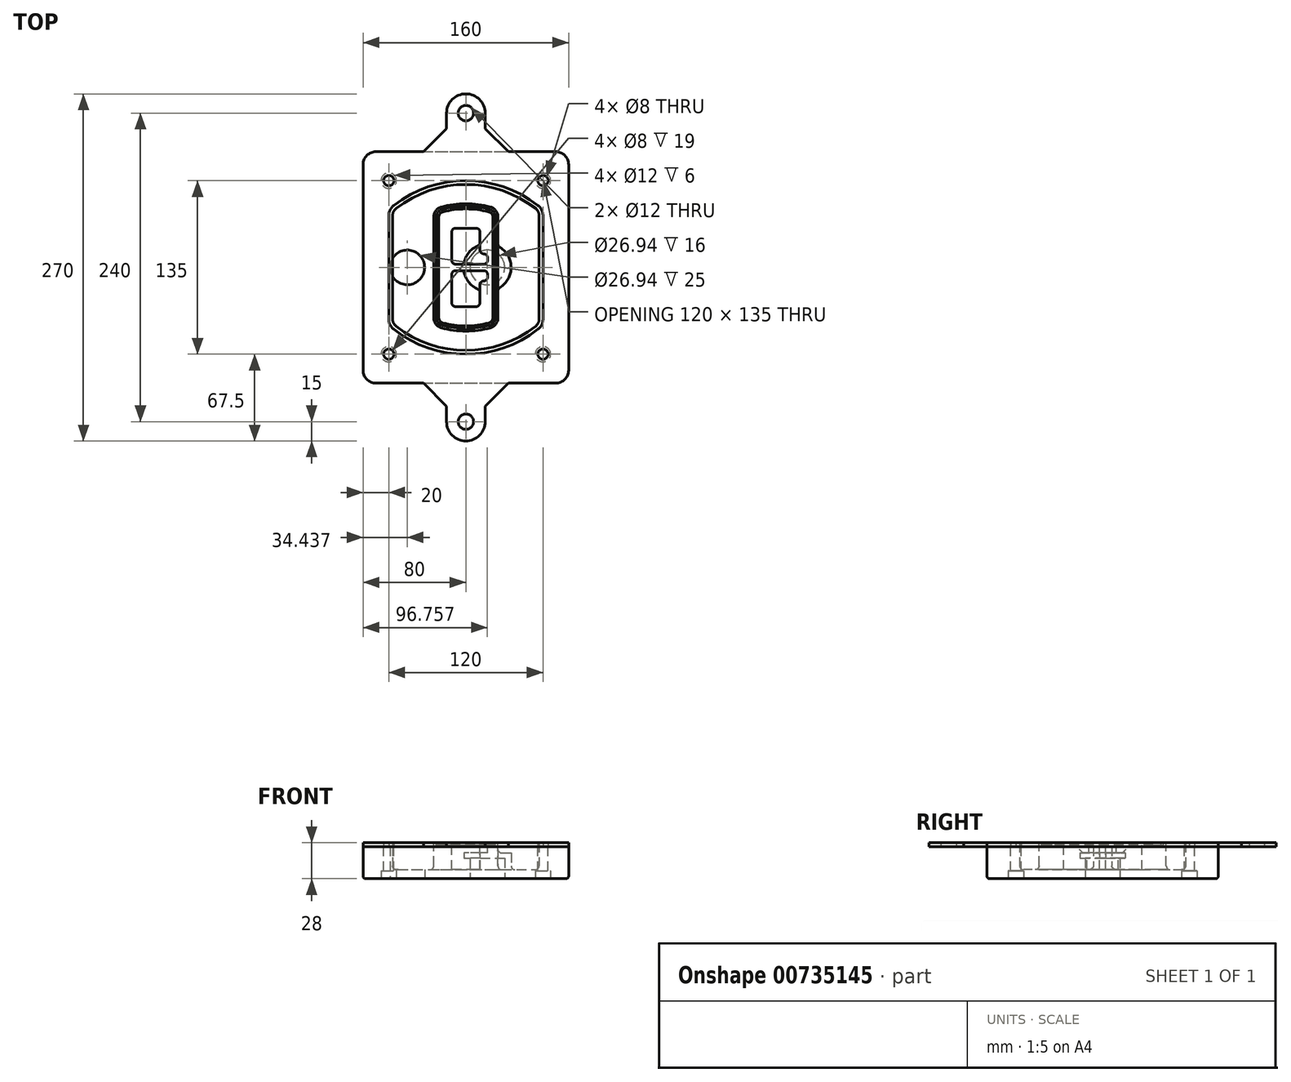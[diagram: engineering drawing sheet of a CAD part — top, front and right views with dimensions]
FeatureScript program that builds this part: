
annotation { "Feature Type Name" : "Feature", "Feature Type Description" : "" }
export const myFeature = defineFeature(function(context is Context, id is Id, definition is map)
    precondition{}
    {
        {
            var Q0;
            Q0=qCreatedBy(makeId("Top.planeOp"),FACE);
            var sketch = newSketch(context, id + "F0", { "sketchPlane" : qUnion([Q0])});
            skPoint(sketch, "E0.rect.middle", {"position": v(0, 0) * mm});
            skLineSegment(sketch, "E1.bottom", {"start": v(-70, -90) * mm, "end": v(70, -90) * mm});
            skLineSegment(sketch, "E1.top", {"start": v(-70, 90) * mm, "end": v(70, 90) * mm});
            skLineSegment(sketch, "E1.left", {"start": v(-80, -80) * mm, "end": v(-80, 80) * mm});
            skLineSegment(sketch, "E1.right", {"start": v(80, -80) * mm, "end": v(80, 80) * mm});
            skLineSegment(sketch, "E2", {"start": v(-80, 90) * mm, "end": v(80, -90) * mm, "construction": true});
            skLineSegment(sketch, "E3", {"start": v(80, 90) * mm, "end": v(-80, -90) * mm, "construction": true});
            skCircle(sketch, "E4", {"center": v(-60, 67.5) * mm, "radius": 4 * mm});
            skCircle(sketch, "E5", {"center": v(60, 67.5) * mm, "radius": 4 * mm});
            skCircle(sketch, "E6", {"center": v(60, -67.5) * mm, "radius": 4 * mm});
            skCircle(sketch, "E7", {"center": v(-60, -67.5) * mm, "radius": 4 * mm});
            skLineSegment(sketch, "E8", {"start": v(-60, 67.5) * mm, "end": v(60, 67.5) * mm, "construction": true});
            skLineSegment(sketch, "E9", {"start": v(60, 67.5) * mm, "end": v(60, -67.5) * mm, "construction": true});
            skLineSegment(sketch, "E10", {"start": v(60, -67.5) * mm, "end": v(-60, -67.5) * mm, "construction": true});
            skLineSegment(sketch, "E11", {"start": v(-60, -67.5) * mm, "end": v(-60, 67.5) * mm, "construction": true});
            skLineSegment(sketch, "E12", {"start": v(-60, 40.3) * mm, "end": v(-60, -40.3) * mm});
            skLineSegment(sketch, "E13", {"start": v(60, 40.3) * mm, "end": v(60, -40.3) * mm});
            skArc(sketch, "E14", {"start": v(56.15, 48.18) * mm, "mid": v(0, 67.5) * mm, "end": v(-56.15, 48.18) * mm});
            skArc(sketch, "E15", {"start": v(-56.15, -48.18) * mm, "mid": v(0, -67.5) * mm, "end": v(56.15, -48.18) * mm});
            skLineSegment(sketch, "E16", {"start": v(-60, 0) * mm, "end": v(60, 0) * mm, "construction": true});
            skPoint(sketch, "E17.visualSharp", {"position": v(-60, -45) * mm});
            skArc(sketch, "E17.filletArc", {"start": v(-60, -40.3) * mm, "mid": v(-58.99, -44.68) * mm, "end": v(-56.15, -48.18) * mm});
            skPoint(sketch, "E18.visualSharp", {"position": v(-60, 45) * mm});
            skArc(sketch, "E18.filletArc", {"start": v(-56.15, 48.18) * mm, "mid": v(-58.99, 44.68) * mm, "end": v(-60, 40.3) * mm});
            skPoint(sketch, "E19.visualSharp", {"position": v(60, 45) * mm});
            skArc(sketch, "E19.filletArc", {"start": v(60, 40.3) * mm, "mid": v(58.99, 44.68) * mm, "end": v(56.15, 48.18) * mm});
            skPoint(sketch, "E20.visualSharp", {"position": v(60, -45) * mm});
            skArc(sketch, "E20.filletArc", {"start": v(56.15, -48.18) * mm, "mid": v(58.99, -44.68) * mm, "end": v(60, -40.3) * mm});
            skPoint(sketch, "E21.visualSharp", {"position": v(-80, 90) * mm});
            skArc(sketch, "E21.filletArc", {"start": v(-70, 90) * mm, "mid": v(-77.07, 87.07) * mm, "end": v(-80, 80) * mm});
            skPoint(sketch, "E22.visualSharp", {"position": v(80, 90) * mm});
            skArc(sketch, "E22.filletArc", {"start": v(80, 80) * mm, "mid": v(77.07, 87.07) * mm, "end": v(70, 90) * mm});
            skPoint(sketch, "E23.visualSharp", {"position": v(80, -90) * mm});
            skArc(sketch, "E23.filletArc", {"start": v(70, -90) * mm, "mid": v(77.07, -87.07) * mm, "end": v(80, -80) * mm});
            skPoint(sketch, "E24.visualSharp", {"position": v(-80, -90) * mm});
            skArc(sketch, "E24.filletArc", {"start": v(-80, -80) * mm, "mid": v(-77.07, -87.07) * mm, "end": v(-70, -90) * mm});
            skArc(sketch, "E25.0", {"start": v(57, 40.3) * mm, "mid": v(56.3, 43.36) * mm, "end": v(54.3, 45.81) * mm});
            skLineSegment(sketch, "E25.1", {"start": v(57, 40.3) * mm, "end": v(57, -40.3) * mm});
            skArc(sketch, "E25.2", {"start": v(54.3, -45.81) * mm, "mid": v(56.3, -43.36) * mm, "end": v(57, -40.3) * mm});
            skArc(sketch, "E25.3", {"start": v(-54.3, -45.81) * mm, "mid": v(0, -64.5) * mm, "end": v(54.3, -45.81) * mm});
            skArc(sketch, "E25.4", {"start": v(-57, -40.3) * mm, "mid": v(-56.3, -43.36) * mm, "end": v(-54.3, -45.81) * mm});
            skArc(sketch, "E25.5", {"start": v(54.3, 45.81) * mm, "mid": v(0, 64.5) * mm, "end": v(-54.3, 45.81) * mm});
            skLineSegment(sketch, "E25.6", {"start": v(-57, 40.3) * mm, "end": v(-57, -40.3) * mm});
            skArc(sketch, "E25.7", {"start": v(-54.3, 45.81) * mm, "mid": v(-56.3, 43.36) * mm, "end": v(-57, 40.3) * mm});
            skArc(sketch, "E26.0", {"start": v(-58.62, 51.33) * mm, "mid": v(-62.58, 46.43) * mm, "end": v(-64, 40.3) * mm});
            skArc(sketch, "E26.1", {"start": v(58.62, 51.33) * mm, "mid": v(0, 71.5) * mm, "end": v(-58.62, 51.33) * mm});
            skArc(sketch, "E26.2", {"start": v(64, 40.3) * mm, "mid": v(62.58, 46.43) * mm, "end": v(58.62, 51.33) * mm});
            skLineSegment(sketch, "E26.3", {"start": v(64, 40.3) * mm, "end": v(64, -40.3) * mm});
            skArc(sketch, "E26.4", {"start": v(58.62, -51.33) * mm, "mid": v(62.58, -46.43) * mm, "end": v(64, -40.3) * mm});
            skLineSegment(sketch, "E26.5", {"start": v(-64, 40.3) * mm, "end": v(-64, -40.3) * mm});
            skArc(sketch, "E26.6", {"start": v(-58.62, -51.33) * mm, "mid": v(0, -71.5) * mm, "end": v(58.62, -51.33) * mm});
            skArc(sketch, "E26.7", {"start": v(-64, -40.3) * mm, "mid": v(-62.58, -46.43) * mm, "end": v(-58.62, -51.33) * mm});
            skSolve(sketch);
        }
        {
            var Q0;
            Q0=makeQuery(id+"F0.imprint","IMPRINT",FACE,{"disambiguationData":[TD([[makeQuery(id+"F0.imprint","IMPRINT",EDGE,{"derivedFrom":sQuery(id+"F0.wireOp",EDGE,"E1.bottom")}),1.0]])]});
            var Q1;
            Q1=makeQuery(id+"F0.imprint","IMPRINT",FACE,{"disambiguationData":[TD([[makeQuery(id+"F0.imprint","IMPRINT",EDGE,{"derivedFrom":sQuery(id+"F0.wireOp",EDGE,"E12")}),1.0]])]});
            var Q2;
            Q2=makeQuery(id+"F0.imprint","IMPRINT",FACE,{"disambiguationData":[TD([[makeQuery(id+"F0.imprint","IMPRINT",EDGE,{"derivedFrom":sQuery(id+"F0.wireOp",EDGE,"E25.0")}),1.0]])]});
            var Q3;
            Q3=makeQuery(id+"F0.imprint","IMPRINT",FACE,{"disambiguationData":[TD([[makeQuery(id+"F0.imprint","IMPRINT",EDGE,{"derivedFrom":sQuery(id+"F0.wireOp",EDGE,"E12")}),-1.0]])]});
            extrude(context, id + "F1", {"entities" : qUnion([Q0, Q1, Q2, Q3]), "oppositeDirection" : true, "depth" : 25 * mm});
        }
        {
            var Q0;
            Q0=makeQuery(id+"F0.imprint","IMPRINT",FACE,{"disambiguationData":[TD([[makeQuery(id+"F0.imprint","IMPRINT",EDGE,{"derivedFrom":sQuery(id+"F0.wireOp",EDGE,"E12")}),1.0]])]});
            extrude(context, id + "F2", {"entities" : qUnion([Q0]), "operationType" : NewBodyOperationType.ADD, "depth" : 3 * mm});
        }
        {
            var Q0;
            Q0=makeQuery(id+"F0.imprint","IMPRINT",FACE,{"disambiguationData":[TD([[makeQuery(id+"F0.imprint","IMPRINT",EDGE,{"derivedFrom":sQuery(id+"F0.wireOp",EDGE,"E25.0")}),1.0]])]});
            extrude(context, id + "F3", {"entities" : qUnion([Q0]), "operationType" : NewBodyOperationType.REMOVE, "oppositeDirection" : true, "depth" : 18 * mm});
        }
        {
            var Q0;
            Q0=makeQuery(id+"F2.opExtrude","CAP_FACE",FACE,{"disambiguationData":[OSD([sQuery(id+"F0.wireOp",EDGE,"E12"),sQuery(id+"F0.wireOp",EDGE,"E13"),sQuery(id+"F0.wireOp",EDGE,"E14"),sQuery(id+"F0.wireOp",EDGE,"E15"),sQuery(id+"F0.wireOp",EDGE,"E17.filletArc"),sQuery(id+"F0.wireOp",EDGE,"E18.filletArc"),sQuery(id+"F0.wireOp",EDGE,"E19.filletArc"),sQuery(id+"F0.wireOp",EDGE,"E20.filletArc"),sQuery(id+"F0.wireOp",EDGE,"E25.0"),sQuery(id+"F0.wireOp",EDGE,"E25.1"),sQuery(id+"F0.wireOp",EDGE,"E25.2"),sQuery(id+"F0.wireOp",EDGE,"E25.3"),sQuery(id+"F0.wireOp",EDGE,"E25.4"),sQuery(id+"F0.wireOp",EDGE,"E25.5"),sQuery(id+"F0.wireOp",EDGE,"E25.6"),sQuery(id+"F0.wireOp",EDGE,"E25.7")])],"isStart":false});
            var sketch = newSketch(context, id + "F4", { "sketchPlane" : qUnion([Q0])});
            skArc(sketch, "E27.0", {"start": v(-19.08, -46.97) * mm, "mid": v(0, -49.5) * mm, "end": v(19.08, -46.97) * mm});
            skArc(sketch, "E28.0", {"start": v(19.08, 46.97) * mm, "mid": v(0, 49.5) * mm, "end": v(-19.08, 46.97) * mm});
            skLineSegment(sketch, "E29", {"start": v(-25, 39.25) * mm, "end": v(-25, -39.25) * mm});
            skLineSegment(sketch, "E30", {"start": v(25, 39.25) * mm, "end": v(25, -39.25) * mm});
            skLineSegment(sketch, "E31", {"start": v(-25, 45.1) * mm, "end": v(25, 45.1) * mm, "construction": true});
            skLineSegment(sketch, "E32", {"start": v(-25, -45.1) * mm, "end": v(25, -45.1) * mm, "construction": true});
            skPoint(sketch, "E33.visualSharp", {"position": v(-25, 45.1) * mm});
            skArc(sketch, "E33.filletArc", {"start": v(-19.08, 46.97) * mm, "mid": v(-23.35, 44.11) * mm, "end": v(-25, 39.25) * mm});
            skPoint(sketch, "E34.visualSharp", {"position": v(25, 45.1) * mm});
            skArc(sketch, "E34.filletArc", {"start": v(25, 39.25) * mm, "mid": v(23.35, 44.11) * mm, "end": v(19.08, 46.97) * mm});
            skPoint(sketch, "E35.visualSharp", {"position": v(25, -45.1) * mm});
            skArc(sketch, "E35.filletArc", {"start": v(19.08, -46.97) * mm, "mid": v(23.35, -44.11) * mm, "end": v(25, -39.25) * mm});
            skPoint(sketch, "E36.visualSharp", {"position": v(-25, -45.1) * mm});
            skArc(sketch, "E36.filletArc", {"start": v(-25, -39.25) * mm, "mid": v(-23.35, -44.11) * mm, "end": v(-19.08, -46.97) * mm});
            skArc(sketch, "E37.0", {"start": v(54.3, 45.81) * mm, "mid": v(0, 64.5) * mm, "end": v(-54.3, 45.81) * mm});
            skArc(sketch, "E37.1", {"start": v(-54.3, 45.81) * mm, "mid": v(-56.3, 43.36) * mm, "end": v(-57, 40.3) * mm});
            skLineSegment(sketch, "E37.2", {"start": v(-57, 40.3) * mm, "end": v(-57, -40.3) * mm});
            skArc(sketch, "E37.3", {"start": v(-57, -40.3) * mm, "mid": v(-56.3, -43.36) * mm, "end": v(-54.3, -45.81) * mm});
            skArc(sketch, "E37.4", {"start": v(-54.3, -45.81) * mm, "mid": v(0, -64.5) * mm, "end": v(54.3, -45.81) * mm});
            skArc(sketch, "E37.5", {"start": v(54.3, -45.81) * mm, "mid": v(56.3, -43.36) * mm, "end": v(57, -40.3) * mm});
            skLineSegment(sketch, "E37.6", {"start": v(57, 40.3) * mm, "end": v(57, -40.3) * mm});
            skArc(sketch, "E37.7", {"start": v(57, 40.3) * mm, "mid": v(56.3, 43.36) * mm, "end": v(54.3, 45.81) * mm});
            skLineSegment(sketch, "E38.0", {"start": v(23, 39.25) * mm, "end": v(23, -39.25) * mm});
            skArc(sketch, "E38.1", {"start": v(18.56, -45.04) * mm, "mid": v(21.76, -42.9) * mm, "end": v(23, -39.25) * mm});
            skArc(sketch, "E38.2", {"start": v(-18.56, -45.04) * mm, "mid": v(0, -47.5) * mm, "end": v(18.56, -45.04) * mm});
            skArc(sketch, "E38.3", {"start": v(-23, -39.25) * mm, "mid": v(-21.76, -42.9) * mm, "end": v(-18.56, -45.04) * mm});
            skLineSegment(sketch, "E38.4", {"start": v(-23, 39.25) * mm, "end": v(-23, -39.25) * mm});
            skArc(sketch, "E38.5", {"start": v(23, 39.25) * mm, "mid": v(21.76, 42.9) * mm, "end": v(18.56, 45.04) * mm});
            skArc(sketch, "E38.6", {"start": v(-18.56, 45.04) * mm, "mid": v(-21.76, 42.9) * mm, "end": v(-23, 39.25) * mm});
            skArc(sketch, "E38.7", {"start": v(18.56, 45.04) * mm, "mid": v(0, 47.5) * mm, "end": v(-18.56, 45.04) * mm});
            skArc(sketch, "E39.0", {"start": v(21, 39.25) * mm, "mid": v(20.18, 41.68) * mm, "end": v(18.04, 43.1) * mm});
            skLineSegment(sketch, "E39.1", {"start": v(21, 39.25) * mm, "end": v(21, -39.25) * mm});
            skArc(sketch, "E39.2", {"start": v(18.04, -43.1) * mm, "mid": v(20.18, -41.68) * mm, "end": v(21, -39.25) * mm});
            skArc(sketch, "E39.3", {"start": v(-18.04, -43.1) * mm, "mid": v(0, -45.5) * mm, "end": v(18.04, -43.1) * mm});
            skArc(sketch, "E39.4", {"start": v(-21, -39.25) * mm, "mid": v(-20.18, -41.68) * mm, "end": v(-18.04, -43.1) * mm});
            skArc(sketch, "E39.5", {"start": v(18.04, 43.1) * mm, "mid": v(0, 45.5) * mm, "end": v(-18.04, 43.1) * mm});
            skLineSegment(sketch, "E39.6", {"start": v(-21, 39.25) * mm, "end": v(-21, -39.25) * mm});
            skArc(sketch, "E39.7", {"start": v(-18.04, 43.1) * mm, "mid": v(-20.18, 41.68) * mm, "end": v(-21, 39.25) * mm});
            skLineSegment(sketch, "E40", {"start": v(-25, 0) * mm, "end": v(25, 0) * mm, "construction": true});
            skLineSegment(sketch, "E41", {"start": v(-11, 5.5) * mm, "end": v(-11, 27.5) * mm});
            skLineSegment(sketch, "E42", {"start": v(-8, 30.5) * mm, "end": v(8, 30.5) * mm});
            skLineSegment(sketch, "E43", {"start": v(11, 27.5) * mm, "end": v(11, 13.5) * mm});
            skLineSegment(sketch, "E44", {"start": v(14, 10.5) * mm, "end": v(14, 10.5) * mm});
            skLineSegment(sketch, "E45", {"start": v(17, 7.5) * mm, "end": v(17, 5.5) * mm});
            skLineSegment(sketch, "E46", {"start": v(14, 2.5) * mm, "end": v(-8, 2.5) * mm});
            skPoint(sketch, "E47.visualSharp", {"position": v(-11, 30.5) * mm});
            skArc(sketch, "E47.filletArc", {"start": v(-8, 30.5) * mm, "mid": v(-10.12, 29.62) * mm, "end": v(-11, 27.5) * mm});
            skPoint(sketch, "E48.visualSharp", {"position": v(11, 30.5) * mm});
            skArc(sketch, "E48.filletArc", {"start": v(11, 27.5) * mm, "mid": v(10.12, 29.62) * mm, "end": v(8, 30.5) * mm});
            skPoint(sketch, "E49.visualSharp", {"position": v(11, 10.5) * mm});
            skArc(sketch, "E49.filletArc", {"start": v(11, 13.5) * mm, "mid": v(11.88, 11.38) * mm, "end": v(14, 10.5) * mm});
            skPoint(sketch, "E50.visualSharp", {"position": v(17, 10.5) * mm});
            skArc(sketch, "E50.filletArc", {"start": v(17, 7.5) * mm, "mid": v(16.12, 9.62) * mm, "end": v(14, 10.5) * mm});
            skPoint(sketch, "E51.visualSharp", {"position": v(17, 2.5) * mm});
            skArc(sketch, "E51.filletArc", {"start": v(14, 2.5) * mm, "mid": v(16.12, 3.38) * mm, "end": v(17, 5.5) * mm});
            skPoint(sketch, "E52.visualSharp", {"position": v(-11, 2.5) * mm});
            skArc(sketch, "E52.filletArc", {"start": v(-11, 5.5) * mm, "mid": v(-10.12, 3.38) * mm, "end": v(-8, 2.5) * mm});
            skLineSegment(sketch, "E53.0.MirrorCS", {"start": v(14, -2.5) * mm, "end": v(-8, -2.5) * mm});
            skArc(sketch, "E54.0.MirrorCS", {"start": v(-11, -5.5) * mm, "mid": v(-10.12, -3.38) * mm, "end": v(-8, -2.5) * mm});
            skLineSegment(sketch, "E55.0.MirrorCS", {"start": v(-11, -5.5) * mm, "end": v(-11, -27.5) * mm});
            skArc(sketch, "E56.0.MirrorCS", {"start": v(-8, -30.5) * mm, "mid": v(-10.12, -29.62) * mm, "end": v(-11, -27.5) * mm});
            skLineSegment(sketch, "E57.0.MirrorCS", {"start": v(-8, -30.5) * mm, "end": v(8, -30.5) * mm});
            skArc(sketch, "E58.0.MirrorCS", {"start": v(11, -27.5) * mm, "mid": v(10.12, -29.62) * mm, "end": v(8, -30.5) * mm});
            skLineSegment(sketch, "E59.0.MirrorCS", {"start": v(11, -27.5) * mm, "end": v(11, -13.5) * mm});
            skArc(sketch, "E60.0.MirrorCS", {"start": v(11, -13.5) * mm, "mid": v(11.88, -11.38) * mm, "end": v(14, -10.5) * mm});
            skArc(sketch, "E61.0.MirrorCS", {"start": v(17, -7.5) * mm, "mid": v(16.12, -9.62) * mm, "end": v(14, -10.5) * mm});
            skLineSegment(sketch, "E62.0.MirrorCS", {"start": v(17, -7.5) * mm, "end": v(17, -5.5) * mm});
            skArc(sketch, "E63.0.MirrorCS", {"start": v(14, -2.5) * mm, "mid": v(16.12, -3.38) * mm, "end": v(17, -5.5) * mm});
            skSolve(sketch);
        }
        {
            var Q0;
            Q0=makeQuery(id+"F4.imprint","IMPRINT",FACE,{"disambiguationData":[TD([[makeQuery(id+"F4.imprint","IMPRINT",EDGE,{"derivedFrom":sQuery(id+"F4.wireOp",EDGE,"E27.0")}),1.0]])]});
            var Q1;
            Q1=makeQuery(id+"F4.imprint","IMPRINT",FACE,{"disambiguationData":[TD([[makeQuery(id+"F4.imprint","IMPRINT",EDGE,{"derivedFrom":sQuery(id+"F4.wireOp",EDGE,"E38.0")}),-1.0]])]});
            var Q2;
            Q2=makeQuery(id+"F4.imprint","IMPRINT",FACE,{"disambiguationData":[TD([[makeQuery(id+"F4.imprint","IMPRINT",EDGE,{"derivedFrom":sQuery(id+"F4.wireOp",EDGE,"E39.0")}),1.0]])]});
            extrude(context, id + "F5", {"entities" : qUnion([Q0, Q1, Q2]), "operationType" : NewBodyOperationType.ADD, "endBound" : BoundingType.UP_TO_NEXT, "oppositeDirection" : true, "depth" : 25 * mm});
        }
        {
            var Q0;
            Q0=makeQuery(id+"F4.imprint","IMPRINT",FACE,{"disambiguationData":[TD([[makeQuery(id+"F4.imprint","IMPRINT",EDGE,{"derivedFrom":sQuery(id+"F4.wireOp",EDGE,"E38.0")}),-1.0]])]});
            extrude(context, id + "F6", {"entities" : qUnion([Q0]), "operationType" : NewBodyOperationType.REMOVE, "oppositeDirection" : true, "depth" : 2 * mm});
        }
        {
            var Q0;
            Q0=makeQuery(id+"F1.opExtrude","CAP_FACE",FACE,{"disambiguationData":[OSD([sQuery(id+"F0.wireOp",EDGE,"E1.bottom"),sQuery(id+"F0.wireOp",EDGE,"E1.top"),sQuery(id+"F0.wireOp",EDGE,"E1.left"),sQuery(id+"F0.wireOp",EDGE,"E1.right"),sQuery(id+"F0.wireOp",EDGE,"E4"),sQuery(id+"F0.wireOp",EDGE,"E5"),sQuery(id+"F0.wireOp",EDGE,"E6"),sQuery(id+"F0.wireOp",EDGE,"E7"),sQuery(id+"F0.wireOp",EDGE,"E21.filletArc"),sQuery(id+"F0.wireOp",EDGE,"E22.filletArc"),sQuery(id+"F0.wireOp",EDGE,"E23.filletArc"),sQuery(id+"F0.wireOp",EDGE,"E24.filletArc")])],"isStart":false});
            var sketch = newSketch(context, id + "F7", { "sketchPlane" : qUnion([Q0])});
            skCircle(sketch, "E64", {"center": v(16.76, 0) * mm, "radius": 13.47 * mm});
            skCircle(sketch, "E65", {"center": v(-45.56, 0) * mm, "radius": 13.47 * mm});
            skLineSegment(sketch, "E66", {"start": v(80, 0) * mm, "end": v(-80, 0) * mm});
            skCircle(sketch, "E67", {"center": v(16.76, 0) * mm, "radius": 18.47 * mm});
            skCircle(sketch, "E68", {"center": v(60, -67.5) * mm, "radius": 6 * mm});
            skCircle(sketch, "E69", {"center": v(-60, -67.5) * mm, "radius": 6 * mm});
            skCircle(sketch, "E70", {"center": v(-60, 67.5) * mm, "radius": 6 * mm});
            skCircle(sketch, "E71", {"center": v(60, 67.5) * mm, "radius": 6 * mm});
            skSolve(sketch);
        }
        {
            var Q0;
            {var subQ1=sQuery(id+"F7.wireOp",EDGE,"E66");var subQ4=sQuery(id+"F7.wireOp",EDGE,"E64");var subQ6=makeQuery(id+"F7.imprint","INTERSECT",VERTEX,{"disambiguationData":[OD(0.0)],"derivedFrom":[subQ4,subQ1]});Q0=makeQuery(id+"F7.imprint","IMPRINT",FACE,{"disambiguationData":[TD([[makeQuery(id+"F7.imprint","IMPRINT",EDGE,{"disambiguationData":[TD([[subQ6,-1.0]])],"derivedFrom":subQ4}),-1.0]])]});}
            var Q1;
            {var subQ0=sQuery(id+"F7.wireOp",EDGE,"E66");var subQ1=sQuery(id+"F7.wireOp",EDGE,"E64");var subQ3=makeQuery(id+"F7.imprint","INTERSECT",VERTEX,{"disambiguationData":[OD(0.0)],"derivedFrom":[subQ1,subQ0]});Q1=makeQuery(id+"F7.imprint","IMPRINT",FACE,{"disambiguationData":[TD([[makeQuery(id+"F7.imprint","IMPRINT",EDGE,{"disambiguationData":[TD([[subQ3,-1.0]])],"derivedFrom":subQ1}),1.0]])]});}
            var Q2;
            {var subQ0=sQuery(id+"F7.wireOp",EDGE,"E66");var subQ1=sQuery(id+"F7.wireOp",EDGE,"E64");var subQ3=makeQuery(id+"F7.imprint","INTERSECT",VERTEX,{"disambiguationData":[OD(0.0)],"derivedFrom":[subQ1,subQ0]});Q2=makeQuery(id+"F7.imprint","IMPRINT",FACE,{"disambiguationData":[TD([[makeQuery(id+"F7.imprint","IMPRINT",EDGE,{"disambiguationData":[TD([[subQ3,1.0]])],"derivedFrom":subQ1}),1.0]])]});}
            var Q3;
            {var subQ1=sQuery(id+"F7.wireOp",EDGE,"E66");var subQ4=sQuery(id+"F7.wireOp",EDGE,"E64");var subQ6=makeQuery(id+"F7.imprint","INTERSECT",VERTEX,{"disambiguationData":[OD(0.0)],"derivedFrom":[subQ4,subQ1]});Q3=makeQuery(id+"F7.imprint","IMPRINT",FACE,{"disambiguationData":[TD([[makeQuery(id+"F7.imprint","IMPRINT",EDGE,{"disambiguationData":[TD([[subQ6,1.0]])],"derivedFrom":subQ4}),-1.0]])]});}
            extrude(context, id + "F8", {"entities" : qUnion([Q0, Q1, Q2, Q3]), "operationType" : NewBodyOperationType.ADD, "oppositeDirection" : true, "depth" : 20 * mm});
        }
        {
            var Q0;
            {var subQ0=sQuery(id+"F7.wireOp",EDGE,"E66");var subQ1=sQuery(id+"F7.wireOp",EDGE,"E64");var subQ3=makeQuery(id+"F7.imprint","INTERSECT",VERTEX,{"disambiguationData":[OD(0.0)],"derivedFrom":[subQ1,subQ0]});Q0=makeQuery(id+"F7.imprint","IMPRINT",FACE,{"disambiguationData":[TD([[makeQuery(id+"F7.imprint","IMPRINT",EDGE,{"disambiguationData":[TD([[subQ3,-1.0]])],"derivedFrom":subQ1}),1.0]])]});}
            var Q1;
            {var subQ0=sQuery(id+"F7.wireOp",EDGE,"E66");var subQ1=sQuery(id+"F7.wireOp",EDGE,"E64");var subQ3=makeQuery(id+"F7.imprint","INTERSECT",VERTEX,{"disambiguationData":[OD(0.0)],"derivedFrom":[subQ1,subQ0]});Q1=makeQuery(id+"F7.imprint","IMPRINT",FACE,{"disambiguationData":[TD([[makeQuery(id+"F7.imprint","IMPRINT",EDGE,{"disambiguationData":[TD([[subQ3,1.0]])],"derivedFrom":subQ1}),1.0]])]});}
            extrude(context, id + "F9", {"entities" : qUnion([Q0, Q1]), "operationType" : NewBodyOperationType.REMOVE, "oppositeDirection" : true, "depth" : 16 * mm});
        }
        {
            var Q0;
            {var subQ0=sQuery(id+"F7.wireOp",EDGE,"E66");var subQ1=sQuery(id+"F7.wireOp",EDGE,"E65");var subQ3=makeQuery(id+"F7.imprint","INTERSECT",VERTEX,{"disambiguationData":[OD(0.0)],"derivedFrom":[subQ1,subQ0]});Q0=makeQuery(id+"F7.imprint","IMPRINT",FACE,{"disambiguationData":[TD([[makeQuery(id+"F7.imprint","IMPRINT",EDGE,{"disambiguationData":[TD([[subQ3,-1.0]])],"derivedFrom":subQ1}),1.0]])]});}
            var Q1;
            {var subQ0=sQuery(id+"F7.wireOp",EDGE,"E66");var subQ1=sQuery(id+"F7.wireOp",EDGE,"E65");var subQ3=makeQuery(id+"F7.imprint","INTERSECT",VERTEX,{"disambiguationData":[OD(0.0)],"derivedFrom":[subQ1,subQ0]});Q1=makeQuery(id+"F7.imprint","IMPRINT",FACE,{"disambiguationData":[TD([[makeQuery(id+"F7.imprint","IMPRINT",EDGE,{"disambiguationData":[TD([[subQ3,1.0]])],"derivedFrom":subQ1}),1.0]])]});}
            extrude(context, id + "F10", {"entities" : qUnion([Q0, Q1]), "operationType" : NewBodyOperationType.REMOVE, "oppositeDirection" : true, "depth" : 25 * mm});
        }
        {
            var Q0;
            Q0=makeQuery(id+"F7.imprint","IMPRINT",FACE,{"disambiguationData":[TD([[makeQuery(id+"F7.imprint","IMPRINT",EDGE,{"derivedFrom":sQuery(id+"F7.wireOp",EDGE,"E68")}),1.0]])]});
            var Q1;
            Q1=makeQuery(id+"F7.imprint","IMPRINT",FACE,{"disambiguationData":[TD([[makeQuery(id+"F7.imprint","IMPRINT",EDGE,{"derivedFrom":makeQuery(id+"F1.opExtrude","CAP_EDGE",EDGE,{"disambiguationData":[OSD([sQuery(id+"F0.wireOp",EDGE,"E5")])],"isStart":false})}),-1.0]])]});
            var Q2;
            Q2=makeQuery(id+"F7.imprint","IMPRINT",FACE,{"disambiguationData":[TD([[makeQuery(id+"F7.imprint","IMPRINT",EDGE,{"derivedFrom":sQuery(id+"F7.wireOp",EDGE,"E69")}),1.0]])]});
            var Q3;
            Q3=makeQuery(id+"F7.imprint","IMPRINT",FACE,{"disambiguationData":[TD([[makeQuery(id+"F7.imprint","IMPRINT",EDGE,{"derivedFrom":makeQuery(id+"F1.opExtrude","CAP_EDGE",EDGE,{"disambiguationData":[OSD([sQuery(id+"F0.wireOp",EDGE,"E4")])],"isStart":false})}),-1.0]])]});
            var Q4;
            Q4=makeQuery(id+"F7.imprint","IMPRINT",FACE,{"disambiguationData":[TD([[makeQuery(id+"F7.imprint","IMPRINT",EDGE,{"derivedFrom":sQuery(id+"F7.wireOp",EDGE,"E70")}),1.0]])]});
            var Q5;
            Q5=makeQuery(id+"F7.imprint","IMPRINT",FACE,{"disambiguationData":[TD([[makeQuery(id+"F7.imprint","IMPRINT",EDGE,{"derivedFrom":makeQuery(id+"F1.opExtrude","CAP_EDGE",EDGE,{"disambiguationData":[OSD([sQuery(id+"F0.wireOp",EDGE,"E7")])],"isStart":false})}),-1.0]])]});
            var Q6;
            Q6=makeQuery(id+"F7.imprint","IMPRINT",FACE,{"disambiguationData":[TD([[makeQuery(id+"F7.imprint","IMPRINT",EDGE,{"derivedFrom":sQuery(id+"F7.wireOp",EDGE,"E71")}),1.0]])]});
            var Q7;
            Q7=makeQuery(id+"F7.imprint","IMPRINT",FACE,{"disambiguationData":[TD([[makeQuery(id+"F7.imprint","IMPRINT",EDGE,{"derivedFrom":makeQuery(id+"F1.opExtrude","CAP_EDGE",EDGE,{"disambiguationData":[OSD([sQuery(id+"F0.wireOp",EDGE,"E6")])],"isStart":false})}),-1.0]])]});
            extrude(context, id + "F11", {"entities" : qUnion([Q0, Q1, Q2, Q3, Q4, Q5, Q6, Q7]), "operationType" : NewBodyOperationType.REMOVE, "oppositeDirection" : true, "depth" : 6 * mm});
        }
        {
            var Q0;
            Q0=makeQuery(id+"F9.boolean.opBoolean","COPY",FACE,{"derivedFrom":makeQuery(id+"F9.opExtrude","CAP_FACE",FACE,{"disambiguationData":[OSD([sQuery(id+"F7.wireOp",EDGE,"E64")])],"isStart":false})});
            var sketch = newSketch(context, id + "F12", { "sketchPlane" : qUnion([Q0])});
            skArc(sketch, "E72.0", {"start": v(11, 17.55) * mm, "mid": v(2.57, 11.82) * mm, "end": v(-1.54, 2.5) * mm});
            skArc(sketch, "E72.1", {"start": v(-1.54, -2.5) * mm, "mid": v(2.57, -11.82) * mm, "end": v(11, -17.55) * mm});
            skLineSegment(sketch, "E73", {"start": v(-1.54, -2.5) * mm, "end": v(14, -2.5) * mm});
            skLineSegment(sketch, "E74.0", {"start": v(14, 2.5) * mm, "end": v(-1.54, 2.5) * mm});
            skArc(sketch, "E74.1", {"start": v(14, 2.5) * mm, "mid": v(16.12, 3.38) * mm, "end": v(17, 5.5) * mm});
            skLineSegment(sketch, "E74.2", {"start": v(17, 7.5) * mm, "end": v(17, 5.5) * mm});
            skArc(sketch, "E74.3", {"start": v(17, 7.5) * mm, "mid": v(16.12, 9.62) * mm, "end": v(14, 10.5) * mm});
            skArc(sketch, "E74.4", {"start": v(11, 13.5) * mm, "mid": v(11.88, 11.38) * mm, "end": v(14, 10.5) * mm});
            skLineSegment(sketch, "E74.5", {"start": v(11, 17.55) * mm, "end": v(11, 13.5) * mm});
            skLineSegment(sketch, "E74.7", {"start": v(14, -2.5) * mm, "end": v(-1.54, -2.5) * mm});
            skArc(sketch, "E74.8", {"start": v(14, -2.5) * mm, "mid": v(16.12, -3.38) * mm, "end": v(17, -5.5) * mm});
            skLineSegment(sketch, "E74.9", {"start": v(17, -7.5) * mm, "end": v(17, -5.5) * mm});
            skArc(sketch, "E74.10", {"start": v(17, -7.5) * mm, "mid": v(16.12, -9.62) * mm, "end": v(14, -10.5) * mm});
            skArc(sketch, "E74.11", {"start": v(11, -13.5) * mm, "mid": v(11.88, -11.38) * mm, "end": v(14, -10.5) * mm});
            skLineSegment(sketch, "E74.12", {"start": v(11, -17.55) * mm, "end": v(11, -13.5) * mm});
            skPoint(sketch, "E75.orphan", {"position": v(11, -27.5) * mm});
            skPoint(sketch, "E76.orphan", {"position": v(-8, -2.5) * mm});
            skPoint(sketch, "E77.orphan", {"position": v(-8, 2.5) * mm});
            skPoint(sketch, "E78.orphan", {"position": v(11, 27.5) * mm});
            skSolve(sketch);
        }
        {
            var Q0;
            {var subQ7=sQuery(id+"F12.wireOp",EDGE,"E72.0");var subQ14=sQuery(id+"F12.wireOp",EDGE,"E72.1");var subQ16=sQuery(id+"F12.wireOp",EDGE,"E74.1");var subQ18=sQuery(id+"F12.wireOp",EDGE,"E74.8");Q0=qUnion([makeQuery(id+"F12.imprint","IMPRINT",FACE,{"disambiguationData":[TD([[makeQuery(id+"F12.imprint","IMPRINT",EDGE,{"derivedFrom":subQ7}),1.0]])]}),makeQuery(id+"F12.imprint","IMPRINT",FACE,{"disambiguationData":[TD([[makeQuery(id+"F12.imprint","IMPRINT",EDGE,{"derivedFrom":subQ14}),1.0]])]}),makeQuery(id+"F12.imprint","IMPRINT",FACE,{"disambiguationData":[TD([[makeQuery(id+"F12.imprint","IMPRINT",EDGE,{"derivedFrom":subQ16}),1.0]])]}),makeQuery(id+"F12.imprint","IMPRINT",FACE,{"disambiguationData":[TD([[makeQuery(id+"F12.imprint","IMPRINT",EDGE,{"derivedFrom":subQ18}),-1.0]])]})]);}
            var Q1;
            Q1=makeQuery(id+"F5.boolean.opBoolean","SPLIT",FACE,{"disambiguationData":[TD([makeQuery(id+"F5.opExtrude","SWEPT_FACE",FACE,{"disambiguationData":[OSD([sQuery(id+"F4.wireOp",EDGE,"E41")])]})])],"derivedFrom":makeQuery(id+"F3.boolean.opBoolean","COPY",FACE,{"derivedFrom":makeQuery(id+"F3.opExtrude","CAP_FACE",FACE,{"disambiguationData":[OSD([sQuery(id+"F0.wireOp",EDGE,"E25.0"),sQuery(id+"F0.wireOp",EDGE,"E25.1"),sQuery(id+"F0.wireOp",EDGE,"E25.2"),sQuery(id+"F0.wireOp",EDGE,"E25.3"),sQuery(id+"F0.wireOp",EDGE,"E25.4"),sQuery(id+"F0.wireOp",EDGE,"E25.5"),sQuery(id+"F0.wireOp",EDGE,"E25.6"),sQuery(id+"F0.wireOp",EDGE,"E25.7")])],"isStart":false})})});
            extrude(context, id + "F13", {"entities" : qUnion([Q0]), "operationType" : NewBodyOperationType.REMOVE, "endBound" : BoundingType.UP_TO_SURFACE, "endBoundEntityFace" : qUnion([Q1]), "depth" : 25 * mm});
        }
        {
            var Q0;
            Q0=makeQuery(id+"F3.boolean.opBoolean","COPY",EDGE,{"derivedFrom":makeQuery(id+"F3.opExtrude","CAP_EDGE",EDGE,{"disambiguationData":[OSD([sQuery(id+"F0.wireOp",EDGE,"E25.6")])],"isStart":false})});
            var Q1;
            Q1=makeQuery(id+"F8.boolean.opBoolean","INTERSECT",EDGE,{"derivedFrom":[makeQuery(id+"F5.opExtrude","SWEPT_FACE",FACE,{"disambiguationData":[OSD([sQuery(id+"F4.wireOp",EDGE,"E30")])]}),makeQuery(id+"F8.opExtrude","CAP_FACE",FACE,{"disambiguationData":[OSD([sQuery(id+"F7.wireOp",EDGE,"E67")])],"isStart":false})]});
            var Q2;
            Q2=makeQuery(id+"F8.boolean.opBoolean","INTERSECT",EDGE,{"disambiguationData":[OD(1.0)],"derivedFrom":[makeQuery(id+"F5.opExtrude","SWEPT_FACE",FACE,{"disambiguationData":[OSD([sQuery(id+"F4.wireOp",EDGE,"E30")])]}),makeQuery(id+"F8.opExtrude","SWEPT_FACE",FACE,{"disambiguationData":[OSD([sQuery(id+"F7.wireOp",EDGE,"E67")])]})]});
            var Q3;
            {var subQ0=sQuery(id+"F4.wireOp",EDGE,"E30");Q3=makeQuery(id+"F8.boolean.opBoolean","SPLIT",EDGE,{"disambiguationData":[TD([makeQuery(id+"F5.opExtrude","SWEPT_FACE",FACE,{"disambiguationData":[OSD([sQuery(id+"F4.wireOp",EDGE,"E35.filletArc")])]})])],"derivedFrom":makeQuery(id+"F5.opExtrude","CAP_EDGE",EDGE,{"disambiguationData":[OSD([subQ0])],"isStart":false})});}
            var Q4;
            {var subQ0=sQuery(id+"F0.wireOp",EDGE,"E25.7");var subQ1=sQuery(id+"F0.wireOp",EDGE,"E25.1");var subQ2=sQuery(id+"F0.wireOp",EDGE,"E25.6");var subQ3=sQuery(id+"F0.wireOp",EDGE,"E25.5");var subQ4=sQuery(id+"F0.wireOp",EDGE,"E25.4");var subQ5=sQuery(id+"F0.wireOp",EDGE,"E25.0");var subQ6=sQuery(id+"F0.wireOp",EDGE,"E25.2");var subQ7=sQuery(id+"F0.wireOp",EDGE,"E25.3");Q4=makeQuery(id+"F8.boolean.opBoolean","INTERSECT",EDGE,{"derivedFrom":[makeQuery(id+"F5.boolean.opBoolean","SPLIT",FACE,{"disambiguationData":[TD([makeQuery(id+"F2.opExtrude","SWEPT_FACE",FACE,{"disambiguationData":[OSD([subQ5])]})])],"derivedFrom":makeQuery(id+"F3.boolean.opBoolean","COPY",FACE,{"derivedFrom":makeQuery(id+"F3.opExtrude","CAP_FACE",FACE,{"disambiguationData":[OSD([subQ5,subQ1,subQ6,subQ7,subQ4,subQ3,subQ2,subQ0])],"isStart":false})})}),makeQuery(id+"F8.opExtrude","SWEPT_FACE",FACE,{"disambiguationData":[OSD([sQuery(id+"F7.wireOp",EDGE,"E67")])]})]});}
            var Q5;
            Q5=makeQuery(id+"F8.boolean.opBoolean","INTERSECT",EDGE,{"disambiguationData":[OD(0.0)],"derivedFrom":[makeQuery(id+"F5.opExtrude","SWEPT_FACE",FACE,{"disambiguationData":[OSD([sQuery(id+"F4.wireOp",EDGE,"E30")])]}),makeQuery(id+"F8.opExtrude","SWEPT_FACE",FACE,{"disambiguationData":[OSD([sQuery(id+"F7.wireOp",EDGE,"E67")])]})]});
            fillet(context, id + "F14", {"entities" : qUnion([Q0, Q1, Q2, Q3, Q4, Q5]), "radius" : 3 * mm, "tangentPropagation" : true, "allowEdgeOverflow" : false});
        }
        {
            var Q0;
            Q0=makeQuery(id+"F1.opExtrude","CAP_EDGE",EDGE,{"disambiguationData":[OSD([sQuery(id+"F0.wireOp",EDGE,"E1.bottom")])],"isStart":false});
            fillet(context, id + "F15", {"entities" : qUnion([Q0]), "radius" : 2 * mm, "tangentPropagation" : true, "allowEdgeOverflow" : false});
        }
        {
            var Q0;
            {var subQ0=sQuery(id+"F0.wireOp",EDGE,"E21.filletArc");var subQ1=sQuery(id+"F0.wireOp",EDGE,"E7");var subQ2=sQuery(id+"F0.wireOp",EDGE,"E6");var subQ3=sQuery(id+"F0.wireOp",EDGE,"E5");var subQ4=sQuery(id+"F0.wireOp",EDGE,"E4");var subQ5=sQuery(id+"F0.wireOp",EDGE,"E22.filletArc");var subQ6=sQuery(id+"F0.wireOp",EDGE,"E1.bottom");var subQ7=sQuery(id+"F0.wireOp",EDGE,"E1.right");var subQ8=sQuery(id+"F0.wireOp",EDGE,"E1.top");var subQ9=sQuery(id+"F0.wireOp",EDGE,"E1.left");var subQ10=sQuery(id+"F0.wireOp",EDGE,"E23.filletArc");var subQ11=sQuery(id+"F0.wireOp",EDGE,"E24.filletArc");Q0=makeQuery(id+"F2.boolean.opBoolean","SPLIT",FACE,{"disambiguationData":[TD([makeQuery(id+"F1.opExtrude","SWEPT_FACE",FACE,{"disambiguationData":[OSD([subQ6])]})])],"derivedFrom":makeQuery(id+"F1.opExtrude","CAP_FACE",FACE,{"disambiguationData":[OSD([subQ6,subQ8,subQ9,subQ7,subQ4,subQ3,subQ2,subQ1,subQ0,subQ5,subQ10,subQ11])],"isStart":true})});}
            var sketch = newSketch(context, id + "F16", { "sketchPlane" : qUnion([Q0])});
            skLineSegment(sketch, "E79", {"start": v(0, 90) * mm, "end": v(0, 120) * mm, "construction": true});
            skCircle(sketch, "E80", {"center": v(0, 120) * mm, "radius": 6 * mm});
            skArc(sketch, "E81", {"start": v(15, 120) * mm, "mid": v(0, 135) * mm, "end": v(-15, 120) * mm});
            skLineSegment(sketch, "E82", {"start": v(15, 120) * mm, "end": v(15, 108) * mm});
            skLineSegment(sketch, "E83", {"start": v(15, 108) * mm, "end": v(33, 90) * mm});
            skLineSegment(sketch, "E84", {"start": v(-15, 120) * mm, "end": v(-15, 108) * mm});
            skLineSegment(sketch, "E85", {"start": v(-15, 108) * mm, "end": v(-33, 90) * mm});
            skArc(sketch, "E86.MirrorCS", {"start": v(-15, 120) * mm, "mid": v(0, 135) * mm, "end": v(15, 120) * mm});
            skLineSegment(sketch, "E87", {"start": v(-80, 0) * mm, "end": v(80, 0) * mm, "construction": true});
            skLineSegment(sketch, "E88.MirrorCS", {"start": v(15, -108) * mm, "end": v(33, -90) * mm});
            skLineSegment(sketch, "E89.MirrorCS", {"start": v(-15, -108) * mm, "end": v(-33, -90) * mm});
            skLineSegment(sketch, "E90.MirrorCS", {"start": v(15, -120) * mm, "end": v(15, -108) * mm});
            skLineSegment(sketch, "E91.MirrorCS", {"start": v(-15, -120) * mm, "end": v(-15, -108) * mm});
            skLineSegment(sketch, "E92.MirrorCS", {"start": v(0, -90) * mm, "end": v(0, -120) * mm, "construction": true});
            skCircle(sketch, "E93.MirrorC", {"center": v(0, -120) * mm, "radius": 6 * mm});
            skArc(sketch, "E94.MirrorCS", {"start": v(15, -120) * mm, "mid": v(0, -135) * mm, "end": v(-15, -120) * mm});
            skSolve(sketch);
        }
        {
            var Q0;
            {var subQ1=sQuery(id+"F16.wireOp",EDGE,"E83");Q0=makeQuery(id+"F16.imprint","IMPRINT",FACE,{"disambiguationData":[TD([[makeQuery(id+"F16.imprint","IMPRINT",EDGE,{"derivedFrom":subQ1}),-1.0]])]});}
            var Q1;
            {var subQ1=sQuery(id+"F16.wireOp",EDGE,"E88.MirrorCS");Q1=makeQuery(id+"F16.imprint","IMPRINT",FACE,{"disambiguationData":[TD([[makeQuery(id+"F16.imprint","IMPRINT",EDGE,{"derivedFrom":subQ1}),1.0]])]});}
            var Q2;
            Q2=makeQuery(id+"F16.imprint","IMPRINT",FACE,{"disambiguationData":[TD([[makeQuery(id+"F16.imprint","IMPRINT",EDGE,{"derivedFrom":makeQuery(id+"F1.opExtrude","CAP_EDGE",EDGE,{"disambiguationData":[OSD([sQuery(id+"F0.wireOp",EDGE,"E1.left")])],"isStart":true})}),-1.0]])]});
            var Q3;
            Q3=makeQuery(id+"F2.opExtrude","CAP_FACE",FACE,{"disambiguationData":[OSD([sQuery(id+"F0.wireOp",EDGE,"E12"),sQuery(id+"F0.wireOp",EDGE,"E13"),sQuery(id+"F0.wireOp",EDGE,"E14"),sQuery(id+"F0.wireOp",EDGE,"E15"),sQuery(id+"F0.wireOp",EDGE,"E17.filletArc"),sQuery(id+"F0.wireOp",EDGE,"E18.filletArc"),sQuery(id+"F0.wireOp",EDGE,"E19.filletArc"),sQuery(id+"F0.wireOp",EDGE,"E20.filletArc"),sQuery(id+"F0.wireOp",EDGE,"E25.0"),sQuery(id+"F0.wireOp",EDGE,"E25.1"),sQuery(id+"F0.wireOp",EDGE,"E25.2"),sQuery(id+"F0.wireOp",EDGE,"E25.3"),sQuery(id+"F0.wireOp",EDGE,"E25.4"),sQuery(id+"F0.wireOp",EDGE,"E25.5"),sQuery(id+"F0.wireOp",EDGE,"E25.6"),sQuery(id+"F0.wireOp",EDGE,"E25.7")])],"isStart":false});
            extrude(context, id + "F17", {"entities" : qUnion([Q0, Q1, Q2]), "endBound" : BoundingType.UP_TO_SURFACE, "depth" : 25 * mm, "endBoundEntityFace" : qUnion([Q3]), "offsetDistance" : 25 * mm});
        }
    });
